# Revit family: Stex 45 Gewindebolzen GB
name_source: partatom
category: HLS-Bauteile
revit_build: Autodesk Revit 2017 (Build: 20190507_1515(x64)
units: mm (PartAtom-declared; Revit-internal decimal feet)

## family parameters
Arbeitsebenenbasiert = Ja
Beim Laden mit Abzugskörper schneiden = Nein
Bemaßung runder Anschluss = Durchmesser verwenden
Gemeinsam genutzt = Ja
Immer vertikal = Nein
Raumberechnungspunkt = Nein
Teiletyp = Normal

## types (15) — shared parameters
Anzugsmoment = 0.00 kN-m
Fabrikat = MEFA
Festigkeitsklasse = 4.6
Firma = MEFA Befestigungs- und Montagesysteme GmbH
Kurztext1 = Stex Gewindebolzen GB 45
Material = Stahl
Mengeneinheit = St
Oberflaeche = galvanisch verzinkt
Profiltyp = 45
Vorgabe-Ansicht = 1219 mm

## per-type parameters (varying)
| type | Abmessung | Artikelnummer | EAN | Gewicht | Gewicht pro Bauteil | Gewinde | Kurztext2 | Länge Gewinde | Länge Gewindestift | Nutzlänge | Sechkantmutter | Zahnplatte Gewinde | vpe |
| Stex 45 Gewindebolzen GB M 8x 50 | M8 x 50 mm | 1281050 | 4250928424730 | 0.13 kg | 0.13 kg | M8 | M8 x 50 mm | 50 mm  [stored 0.164042 ft] | MEFA Gewindestifte : Gewindestift M 8x 50 | 23 mm | MEFA Sechskantmutter : Sechskantmutter M 8 | MEFA Zahnplatte 34x21 für Stex 45 : MEFA Zahnplatte 34x21 für Stex 45 M 8 | 40 St |
| Stex 45 Gewindebolzen GB M 8x 70 | M8 x 70 mm | 1281070 | 4250928424747 | 0.14 kg | 0.14 kg | M8 | M8 x 70 mm | 70 mm  [stored 0.229659 ft] | MEFA Gewindestifte : Gewindestift M 8x 70 | 43 mm | MEFA Sechskantmutter : Sechskantmutter M 8 | MEFA Zahnplatte 34x21 für Stex 45 : MEFA Zahnplatte 34x21 für Stex 45 M 8 | 20 St |
| Stex 45 Gewindebolzen GB M 8x 90 | M8 x 90 mm | 1281090 | 4250928424754 | 0.15 kg | 0.15 kg | M8 | M8 x 90 mm | 90 mm  [stored 0.295276 ft] | MEFA Gewindestifte : Gewindestift M 8x 90 | 63 mm | MEFA Sechskantmutter : Sechskantmutter M 8 | MEFA Zahnplatte 34x21 für Stex 45 : MEFA Zahnplatte 34x21 für Stex 45 M 8 | 20 St |
| Stex 45 Gewindebolzen GB M 8x110 | M8 x 110 mm | 1281110 | 4250928424761 | 0.15 kg | 0.15 kg | M8 | M8 x 110 mm | 110 mm  [stored 0.360892 ft] | MEFA Gewindestifte : Gewindestift M 8x110 | 83 mm | MEFA Sechskantmutter : Sechskantmutter M 8 | MEFA Zahnplatte 34x21 für Stex 45 : MEFA Zahnplatte 34x21 für Stex 45 M 8 | 20 St |
| Stex 45 Gewindebolzen GB M 8x130 | M8 x 130 mm | 1281130 | 4250928424778 | 0.16 kg | 0.16 kg | M8 | M8 x 130 mm | 130 mm  [stored 0.426509 ft] | MEFA Gewindestifte : Gewindestift M 8x130 | 103 mm | MEFA Sechskantmutter : Sechskantmutter M 8 | MEFA Zahnplatte 34x21 für Stex 45 : MEFA Zahnplatte 34x21 für Stex 45 M 8 | 20 St |
| Stex 45 Gewindebolzen GB M10x 50 | M10 x 50 mm | 1282050 | 4250928424785 | 0.15 kg | 0.15 kg | M10 | M10 x 50 mm | 50 mm  [stored 0.164042 ft] | MEFA Gewindestifte : Gewindestift M10x 50 | 23 mm | MEFA Sechskantmutter : Sechskantmutter M10 | MEFA Zahnplatte 34x21 für Stex 45 : MEFA Zahnplatte 34x21 für Stex 45 M10 | 40 St |
| Stex 45 Gewindebolzen GB M10x 70 | M10 x 70 mm | 1282070 | 4250928424792 | 0.16 kg | 0.16 kg | M10 | M10 x 70 mm | 70 mm  [stored 0.229659 ft] | MEFA Gewindestifte : Gewindestift M10x 70 | 43 mm | MEFA Sechskantmutter : Sechskantmutter M10 | MEFA Zahnplatte 34x21 für Stex 45 : MEFA Zahnplatte 34x21 für Stex 45 M10 | 20 St |
| Stex 45 Gewindebolzen GB M10x 90 | M10 x 90 mm | 1282090 | 4250928424808 | 0.17 kg | 0.17 kg | M10 | M10 x 90 mm | 90 mm  [stored 0.295276 ft] | MEFA Gewindestifte : Gewindestift M10x 90 | 63 mm | MEFA Sechskantmutter : Sechskantmutter M10 | MEFA Zahnplatte 34x21 für Stex 45 : MEFA Zahnplatte 34x21 für Stex 45 M10 | 20 St |
| Stex 45 Gewindebolzen GB M10x110 | M10 x 110 mm | 1282110 | 4250928424815 | 0.18 kg | 0.18 kg | M10 | M10 x 110 mm | 110 mm  [stored 0.360892 ft] | MEFA Gewindestifte : Gewindestift M10x110 | 83 mm | MEFA Sechskantmutter : Sechskantmutter M10 | MEFA Zahnplatte 34x21 für Stex 45 : MEFA Zahnplatte 34x21 für Stex 45 M10 | 20 St |
| Stex 45 Gewindebolzen GB M10x130 | M10 x 130 mm | 1282130 | 4250928424822 | 0.19 kg | 0.19 kg | M10 | M10 x 130 mm | 130 mm  [stored 0.426509 ft] | MEFA Gewindestifte : Gewindestift M10x130 | 103 mm | MEFA Sechskantmutter : Sechskantmutter M10 | MEFA Zahnplatte 34x21 für Stex 45 : MEFA Zahnplatte 34x21 für Stex 45 M10 | 20 St |
| Stex 45 Gewindebolzen GB M12x 50 | M12 x 50 mm | 1283050 | 4250928424839 | 0.16 kg | 0.16 kg | M12 | M12 x 50 mm | 50 mm  [stored 0.164042 ft] | MEFA Gewindestifte : Gewindestift M12x 50 | 23 mm | MEFA Sechskantmutter : Sechskantmutter M12 | MEFA Zahnplatte 34x21 für Stex 45 : MEFA Zahnplatte 34x21 für Stex 45 M12 | 40 St |
| Stex 45 Gewindebolzen GB M12x 70 | M12 x 70 mm | 1283070 | 4250928424846 | 0.17 kg | 0.17 kg | M12 | M12 x 70 mm | 70 mm  [stored 0.229659 ft] | MEFA Gewindestifte : Gewindestift M12x 70 | 43 mm | MEFA Sechskantmutter : Sechskantmutter M12 | MEFA Zahnplatte 34x21 für Stex 45 : MEFA Zahnplatte 34x21 für Stex 45 M12 | 20 St |
| Stex 45 Gewindebolzen GB M12x 90 | M12 x 90 mm | 1283090 | 4250928424853 | 0.19 kg | 0.19 kg | M12 | M12 x 90 mm | 90 mm  [stored 0.295276 ft] | MEFA Gewindestifte : Gewindestift M12x 90 | 63 mm | MEFA Sechskantmutter : Sechskantmutter M12 | MEFA Zahnplatte 34x21 für Stex 45 : MEFA Zahnplatte 34x21 für Stex 45 M12 | 20 St |
| Stex 45 Gewindebolzen GB M12x110 | M12 x 110 mm | 1283110 | 4250928424860 | 0.20 kg | 0.20 kg | M12 | M12 x 110 mm | 110 mm  [stored 0.360892 ft] | MEFA Gewindestifte : Gewindestift M12x110 | 83 mm | MEFA Sechskantmutter : Sechskantmutter M12 | MEFA Zahnplatte 34x21 für Stex 45 : MEFA Zahnplatte 34x21 für Stex 45 M12 | 20 St |
| Stex 45 Gewindebolzen GB M12x130 | M12 x 130 mm | 1283130 | 4250928424877 | 0.22 kg | 0.22 kg | M12 | M12 x 130 mm | 130 mm  [stored 0.426509 ft] | MEFA Gewindestifte : Gewindestift M12x130 | 103 mm | MEFA Sechskantmutter : Sechskantmutter M12 | MEFA Zahnplatte 34x21 für Stex 45 : MEFA Zahnplatte 34x21 für Stex 45 M12 | 20 St |

note: [stored X ft] marks values corroborated as IEEE doubles in the binary element streams (Revit-internal decimal feet)

## geometry (parser evidence)
native form markers: Sweep x3
no freeform markers — native parametric forms only
